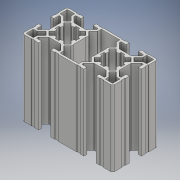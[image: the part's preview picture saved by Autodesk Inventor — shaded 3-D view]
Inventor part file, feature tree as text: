
AUTODESK INVENTOR PART (.ipt)
format: ipt  version: 2018 (Build 220112000, 112)  size: 571,904 bytes
history: native  units: mm
features: other x1, extrude x1, sketch x1
ambient origin geometry x8: Origin, YZ Plane, XZ Plane, XY Plane, X Axis, Y Axis, Z Axis, Center Point
bodies: Body1 (feature_tree)
feature tree (3):
  other  "Sólido1"
  extrude  "Extrusão1"  [1 undecoded]
  sketch  "Esboço1"  dims[d0=50.0mm d1=0.0mm]
note: 1 required parameter value undecoded (feature->parameter linkage not recoverable at this tier; creation-order binding heuristic only, values carry confidence <= 0.55)
